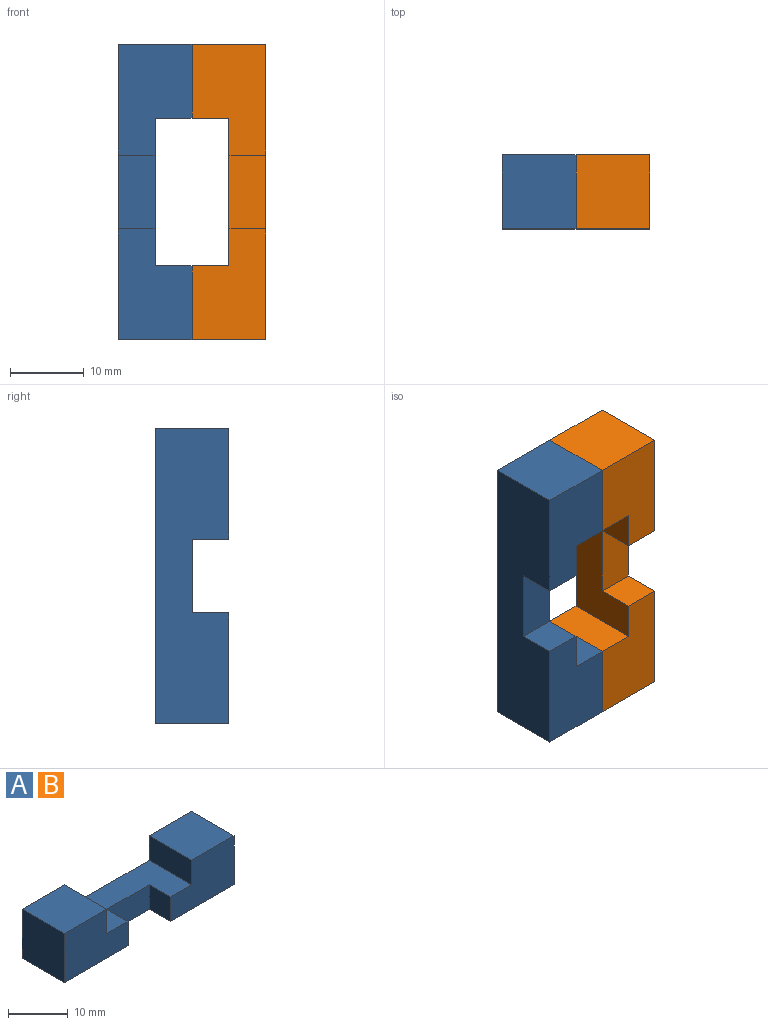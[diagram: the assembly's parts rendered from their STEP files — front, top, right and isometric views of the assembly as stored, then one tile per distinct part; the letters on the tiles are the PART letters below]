
ASSEMBLY  parts=2 mates=1
PART A: 14 faces, bbox 40x10x10 mm
  f0: plane 15x10mm, normal (0,-1,0), area 125mm2, adj f1,f3,f6,f9,f10,f11
  f1: plane 40x10mm, normal (0,0,-1), area 350mm2, adj f0,f2,f4,f5,f6,f11,f12,f13
  f2: plane 15x10mm, normal (0,-1,0), area 125mm2, adj f1,f5,f7,f8,f9,f12
  f3: plane 10x10mm, normal (0,0,1), area 100mm2, adj f0,f4,f6,f10
  f4: plane 40x10mm, normal (0,1,0), area 300mm2, adj f1,f3,f5,f6,f7,f8,f9,f10
  f5: plane 10x10mm, normal (-1,0,0), area 100mm2, adj f1,f2,f4,f7
  f6: plane 10x10mm, normal (1,0,0), area 100mm2, adj f0,f1,f3,f4
  f7: plane 10x10mm, normal (0,0,1), area 100mm2, adj f2,f4,f5,f8
  f8: plane 10x5mm, normal (1,0,0), area 50mm2, adj f2,f4,f7,f9
  f9: plane 20x10mm, normal (0,0,1), area 150mm2, adj f0,f2,f4,f8,f10,f11,f12,f13
  f10: plane 10x5mm, normal (-1,0,0), area 50mm2, adj f0,f3,f4,f9
  f11: plane 5x5mm, normal (-1,0,0), area 25mm2, adj f0,f1,f9,f13
  f12: plane 5x5mm, normal (1,0,0), area 25mm2, adj f1,f2,f9,f13
  f13: plane 10x5mm, normal (0,-1,0), area 50mm2, adj f1,f9,f11,f12
PART B: same geometry as A
PLACE A rot(axis=(0,1,0),90deg) t=(-10,5,20)mm
PLACE B rot(axis=(0,-1,0),90deg) t=(10,5,20)mm
MATE fastened B.f3 <-> A.f7  axis (-1,0,0) through (0,5,35)mm
